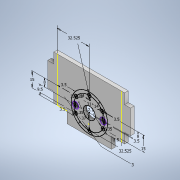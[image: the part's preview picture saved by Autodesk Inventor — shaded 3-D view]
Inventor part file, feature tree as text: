
AUTODESK INVENTOR PART (.ipt)
format: ipt  version: 2022 (Build 260153000, 153)  size: 196,096 bytes
history: native  units: mm
features: sketch x7, extrude x6
ambient origin geometry x8: Origin, YZ Plane, XZ Plane, XY Plane, X Axis, Y Axis, Z Axis, Center Point
bodies: Solid1 (feature_tree)
feature tree (13):
  extrude  "Extrusion1"  Depth=11.25mm
  sketch  "Sketch2"  dims[d2=10.0mm d3=45.0mm]
  sketch  "Sketch3"  dims[d4=45.0mm d5=10.0mm]
  extrude  "Extrusion2"  Depth=45.0mm
  sketch  "Sketch4"  dims[d6=65.05mm d7=3.7mm d8=0.0mm]
  extrude  "Extrusion4"  Depth=10.0mm
  extrude  "Extrusion5"  Depth=3.7mm TaperAngle=0.0deg
  sketch  "Sketch5"  dims[d9=12.1mm d10=32.525mm]
  extrude  "Extrusion6"  Depth=32.525mm
  extrude  "Extrusion7"  Depth=6.35mm
  sketch  "Sketch1"  dims[d0=45.05mm d1=11.25mm]
  sketch  "Sketch6"  dims[d11=9.5mm d12=6.35mm]
  sketch  "Sketch7"  dims[d13=14.0mm d14=6.35mm d15=14.0mm d16=5.0mm d17=0.0mm d20=31.0mm d21=3.5mm d22=32.525mm d23=3.0mm d24=32.525mm d25=3.5mm d26=8.0mm d27=3.5mm d28=3.5mm d29=3.5mm d30=8.0mm d31=15.0mm d32=3.5mm d33=0.0mm d34=5.0mm d35=0.0mm d36=37.0mm d37=0.0mm d38=0.0mm d39=0.0mm d40=3.39mm d41=3.39mm d42=0.0mm d43=0.0mm d44=0.0mm d45=3.7mm d46=0.0mm d47=10.32mm d48=10.32mm d49=6.085mm d50=10.32mm d51=6.085mm d52=3.7mm d53=0.0mm d54=15.0mm d18=0.5mm d19=0.872665mm]
